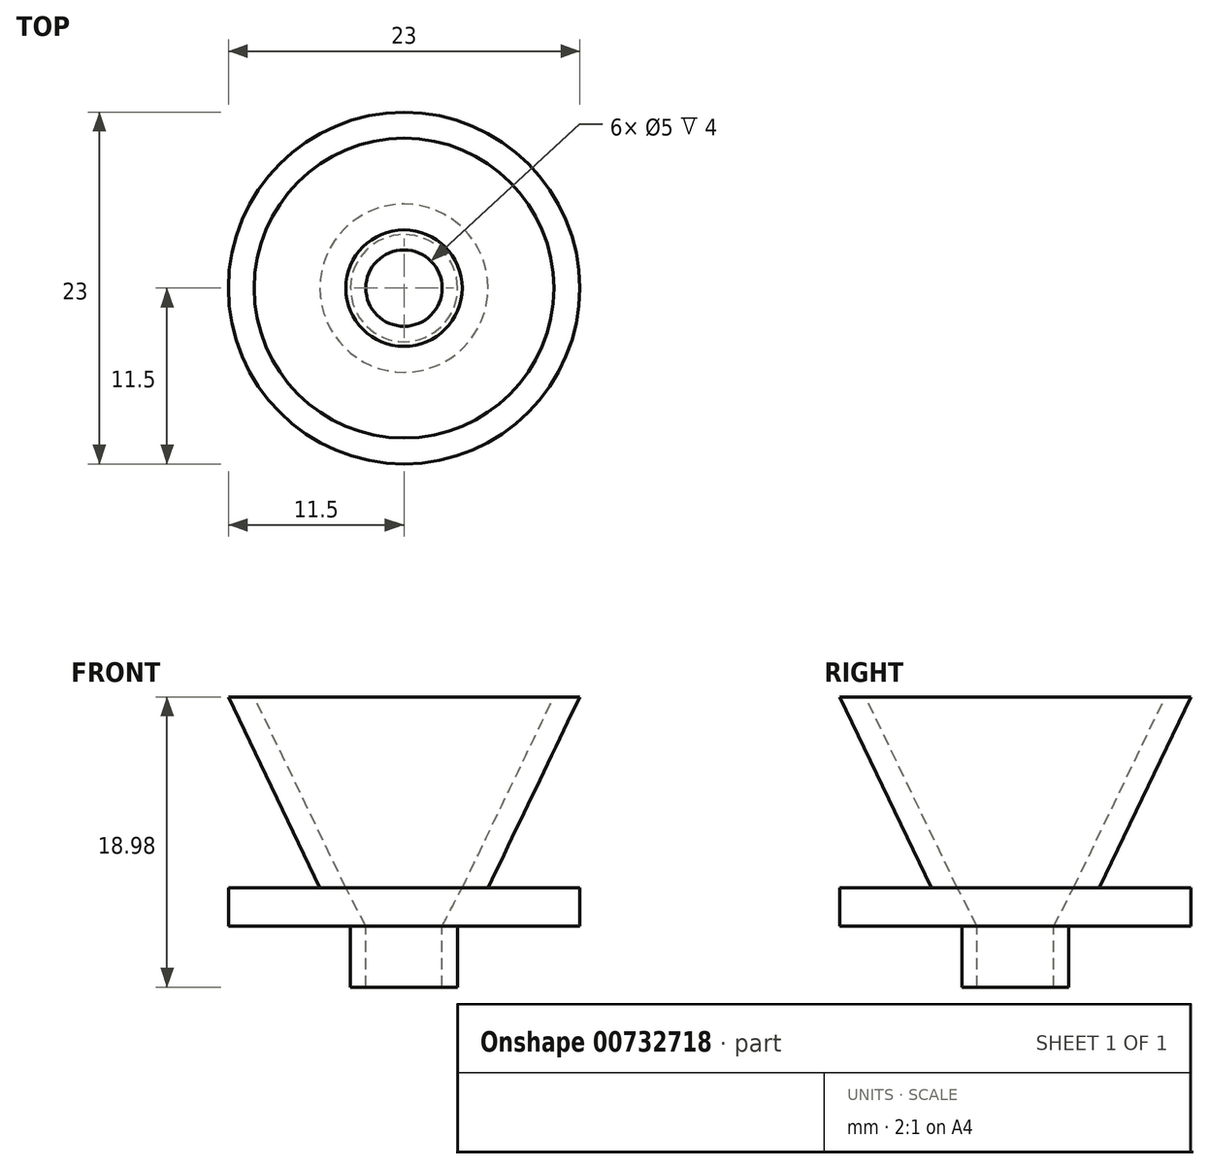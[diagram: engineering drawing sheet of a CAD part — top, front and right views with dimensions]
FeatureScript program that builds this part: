
annotation { "Feature Type Name" : "Feature", "Feature Type Description" : "" }
export const myFeature = defineFeature(function(context is Context, id is Id, definition is map)
    precondition{}
    {
        {
            var Q0;
            Q0=qCreatedBy(makeId("Front.planeOp"),FACE);
            var sketch = newSketch(context, id + "F0", { "sketchPlane" : qUnion([Q0])});
            skLineSegment(sketch, "E0", {"start": v(-2.5, 0) * mm, "end": v(-2.5, -4) * mm});
            skLineSegment(sketch, "E1", {"start": v(-2.5, -4) * mm, "end": v(-3.5, -4) * mm});
            skLineSegment(sketch, "E2", {"start": v(-3.5, -4) * mm, "end": v(-3.5, 0) * mm});
            skLineSegment(sketch, "E3", {"start": v(-3.5, 0) * mm, "end": v(-11.5, 0) * mm});
            skLineSegment(sketch, "E4", {"start": v(-11.5, 0) * mm, "end": v(-11.5, 2.5) * mm});
            skLineSegment(sketch, "E5", {"start": v(-11.5, 2.5) * mm, "end": v(-5.5, 2.5) * mm});
            skLineSegment(sketch, "E6", {"start": v(-5.5, 2.5) * mm, "end": v(-11.5, 14.98) * mm});
            skLineSegment(sketch, "E7", {"start": v(-11.5, 14.98) * mm, "end": v(-9.8, 14.98) * mm});
            skLineSegment(sketch, "E8", {"start": v(-9.8, 14.98) * mm, "end": v(-3.8, 2.5) * mm});
            skLineSegment(sketch, "E9", {"start": v(-3.8, 2.5) * mm, "end": v(-2.5, 0) * mm});
            skLineSegment(sketch, "E10", {"start": v(0, 15.43) * mm, "end": v(0, 0) * mm});
            skSolve(sketch);
        }
        {
            var Q0;
            Q0=makeQuery(id+"F0.imprint","IMPRINT",FACE,{"disambiguationData":[TD([[makeQuery(id+"F0.imprint","IMPRINT",EDGE,{"derivedFrom":sQuery(id+"F0.wireOp",EDGE,"E0")}),-1.0]])]});
            var Q1;
            Q1=sQuery(id+"F0.wireOp",EDGE,"E10");
            revolve(context, id + "F1", {"surfaceOperationType" : NewSurfaceOperationType.NEW, "entities" : qUnion([Q0]), "axis" : qUnion([Q1]), "revolveType" : RevolveType.FULL});
        }
    });
